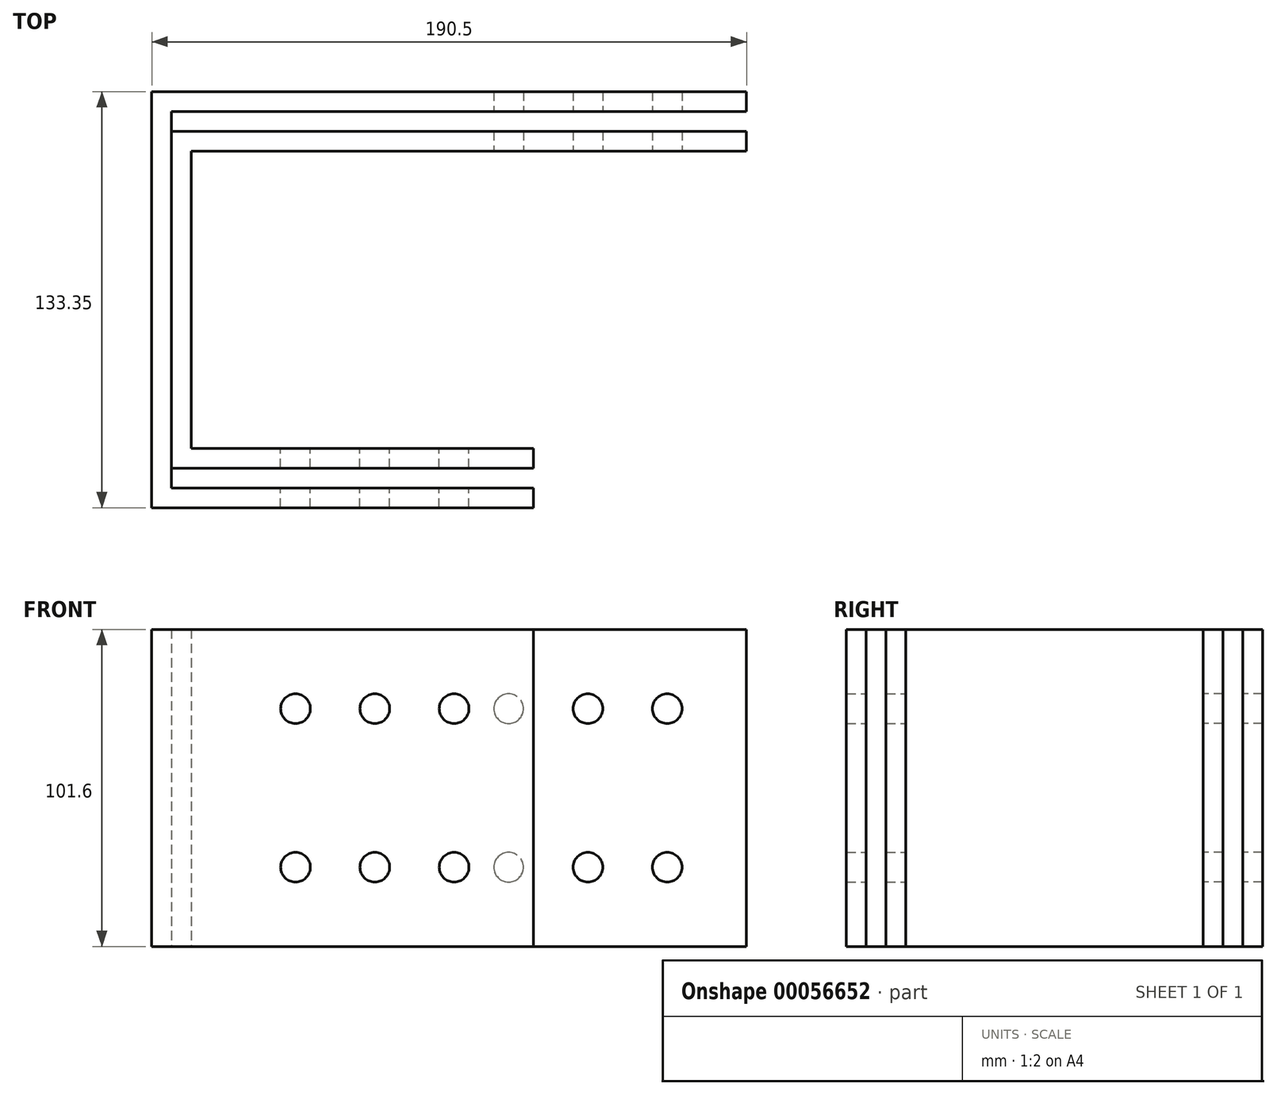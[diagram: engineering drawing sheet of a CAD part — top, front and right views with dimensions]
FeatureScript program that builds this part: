
annotation { "Feature Type Name" : "Feature", "Feature Type Description" : "" }
export const myFeature = defineFeature(function(context is Context, id is Id, definition is map)
    precondition{}
    {
        {
            var Q0;
            Q0=qCreatedBy(makeId("Top.planeOp"),FACE);
            var sketch = newSketch(context, id + "F0", { "sketchPlane" : qUnion([Q0])});
            skLineSegment(sketch, "E0", {"start": v(103.44, 55.58) * mm, "end": v(-74.36, 55.58) * mm});
            skLineSegment(sketch, "E1", {"start": v(-74.36, 55.58) * mm, "end": v(-74.36, -39.67) * mm});
            skLineSegment(sketch, "E2", {"start": v(-74.36, -39.67) * mm, "end": v(35.18, -39.67) * mm});
            skLineSegment(sketch, "E3", {"start": v(35.18, -39.67) * mm, "end": v(35.18, -46.02) * mm});
            skLineSegment(sketch, "E4", {"start": v(35.18, -46.02) * mm, "end": v(-80.71, -46.02) * mm});
            skLineSegment(sketch, "E5", {"start": v(-80.71, -46.02) * mm, "end": v(-80.71, 61.93) * mm});
            skLineSegment(sketch, "E6", {"start": v(-80.71, 61.93) * mm, "end": v(103.44, 61.93) * mm});
            skLineSegment(sketch, "E7", {"start": v(103.44, 61.93) * mm, "end": v(103.44, 55.58) * mm});
            skSolve(sketch);
        }
        {
            var Q0;
            Q0 = qSketchRegion(id + "F0", true);
            extrude(context, id + "F1", {"entities" : qUnion([Q0]), "endBound" : BoundingType.SYMMETRIC, "depth" : 101.6 * mm});
        }
        {
            var Q0;
            Q0=qCreatedBy(makeId("Top.planeOp"),FACE);
            var sketch = newSketch(context, id + "F2", { "sketchPlane" : qUnion([Q0])});
            skLineSegment(sketch, "E8", {"start": v(103.44, 68.28) * mm, "end": v(-80.71, 68.28) * mm});
            skLineSegment(sketch, "E9", {"start": v(-80.71, 68.28) * mm, "end": v(-80.71, -52.37) * mm});
            skLineSegment(sketch, "E10", {"start": v(-80.71, -52.37) * mm, "end": v(35.18, -52.37) * mm});
            skLineSegment(sketch, "E11", {"start": v(35.18, -52.37) * mm, "end": v(35.18, -58.72) * mm});
            skLineSegment(sketch, "E12", {"start": v(35.18, -58.72) * mm, "end": v(-87.06, -58.72) * mm});
            skLineSegment(sketch, "E13", {"start": v(-87.06, -58.72) * mm, "end": v(-87.06, 74.63) * mm});
            skLineSegment(sketch, "E14", {"start": v(-87.06, 74.63) * mm, "end": v(103.44, 74.63) * mm});
            skLineSegment(sketch, "E15", {"start": v(103.44, 74.63) * mm, "end": v(103.44, 68.28) * mm});
            skSolve(sketch);
        }
        {
            var Q0;
            Q0 = qSketchRegion(id + "F2", true);
            extrude(context, id + "F3", {"entities" : qUnion([Q0]), "endBound" : BoundingType.SYMMETRIC, "depth" : 101.6 * mm});
        }
        {
            var Q0;
            Q0=qCreatedBy(makeId("Front.planeOp"),FACE);
            var sketch = newSketch(context, id + "F4", { "sketchPlane" : qUnion([Q0])});
            skCircle(sketch, "E16", {"center": v(78.04, 25.4) * mm, "radius": 4.76 * mm});
            skCircle(sketch, "E17.0.1.0", {"center": v(78.04, -25.4) * mm, "radius": 4.76 * mm});
            skCircle(sketch, "E17.1.0.0", {"center": v(52.64, 25.4) * mm, "radius": 4.76 * mm});
            skCircle(sketch, "E17.1.1.0", {"center": v(52.64, -25.4) * mm, "radius": 4.76 * mm});
            skCircle(sketch, "E17.2.0.0", {"center": v(27.24, 25.4) * mm, "radius": 4.76 * mm});
            skCircle(sketch, "E17.2.1.0", {"center": v(27.24, -25.4) * mm, "radius": 4.76 * mm});
            skLineSegment(sketch, "E17.direction1", {"start": v(78.04, 25.4) * mm, "end": v(52.64, 25.4) * mm, "construction": true});
            skLineSegment(sketch, "E17.direction2", {"start": v(78.04, 25.4) * mm, "end": v(78.04, -25.4) * mm, "construction": true});
            skSolve(sketch);
        }
        {
            var Q0;
            Q0 = qSketchRegion(id + "F4", true);
            var Q1;
            Q1=makeQuery(id+"F1.opExtrude","SWEPT_FACE",FACE,{"disambiguationData":[OSD([sQuery(id+"F0.wireOp",EDGE,"E6")])]});
            extrude(context, id + "F5", {"entities" : qUnion([Q0]), "operationType" : NewBodyOperationType.REMOVE, "endBound" : BoundingType.THROUGH_ALL, "oppositeDirection" : true, "endBoundEntityFace" : qUnion([Q1]), "depth" : 25.4 * mm});
        }
        {
            var Q0;
            Q0=qCreatedBy(makeId("Front.planeOp"),FACE);
            var sketch = newSketch(context, id + "F6", { "sketchPlane" : qUnion([Q0])});
            skCircle(sketch, "E18", {"center": v(9.78, 25.4) * mm, "radius": 4.76 * mm});
            skCircle(sketch, "E19.0.1.0", {"center": v(9.78, -25.4) * mm, "radius": 4.76 * mm});
            skCircle(sketch, "E19.1.0.0", {"center": v(-15.62, 25.4) * mm, "radius": 4.76 * mm});
            skCircle(sketch, "E19.1.1.0", {"center": v(-15.62, -25.4) * mm, "radius": 4.76 * mm});
            skCircle(sketch, "E19.2.0.0", {"center": v(-41.02, 25.4) * mm, "radius": 4.76 * mm});
            skCircle(sketch, "E19.2.1.0", {"center": v(-41.02, -25.4) * mm, "radius": 4.76 * mm});
            skLineSegment(sketch, "E19.direction1", {"start": v(9.78, 25.4) * mm, "end": v(-15.62, 25.4) * mm, "construction": true});
            skLineSegment(sketch, "E19.direction2", {"start": v(9.78, 25.4) * mm, "end": v(9.78, -25.4) * mm, "construction": true});
            skSolve(sketch);
        }
        {
            var Q0;
            Q0 = qSketchRegion(id + "F6", true);
            extrude(context, id + "F7", {"entities" : qUnion([Q0]), "operationType" : NewBodyOperationType.REMOVE, "endBound" : BoundingType.THROUGH_ALL, "depth" : 25.4 * mm});
        }
    });
